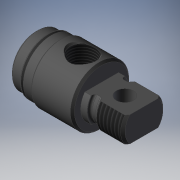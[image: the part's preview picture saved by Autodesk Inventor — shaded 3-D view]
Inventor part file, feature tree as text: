
AUTODESK INVENTOR PART (.ipt)
format: ipt  version: 2019 (Build 230136000, 136)  size: 330,752 bytes
history: native  units: in
note: dims shown in document units (in); Inventor stores cm internally (conversion verified against a paired STEP export)
features: other x168, sketch x7, revolve x4, thread x2, extrude x2, hole x1
ambient origin geometry x8: Origin, YZ Plane, XZ Plane, XY Plane, X Axis, Y Axis, Z Axis, Center Point
bodies: Solid1 (feature_tree)
feature tree (184):
  revolve  "Revolution1"  Angle=360.0deg
  revolve  "Revolution2"  [1 undecoded]
  thread  "Thread1"  [1 undecoded]
  extrude  "Extrusion1"  TaperAngle=360.0deg  [1 undecoded]
  hole  "Hole1"  [1 undecoded]
  revolve  "Revolution3"  [1 undecoded]
  thread  "Thread2"  [1 undecoded]
  revolve  "Revolution4"  [1 undecoded]
  extrude  "Extrusion2"  [1 undecoded]
  other  "1_XY"
  other  "1_YZ"
  other  "1_ZX"
  other  "1_X"
  other  "1_Y"
  other  "1_Z"
  other  "1_Center"
  other  "c1_XY"
  other  "c1_YZ"
  other  "c1_ZX"
  other  "c1_X"
  other  "c1_Y"
  other  "c1_Z"
  other  "c1_Center"
  other  "c2_XY"
  other  "c2_YZ"
  other  "c2_ZX"
  other  "c2_X"
  other  "c2_Y"
  other  "c2_Z"
  other  "c2_Center"
  other  "cc1_XY"
  other  "cc1_YZ"
  other  "cc1_ZX"
  other  "cc1_X"
  other  "cc1_Y"
  other  "cc1_Z"
  other  "cc1_Center"
  other  "cc2_XY"
  other  "cc2_YZ"
  other  "cc2_ZX"
  other  "cc2_X"
  other  "cc2_Y"
  other  "cc2_Z"
  other  "cc2_Center"
  other  "lovra1_XY"
  other  "lovra1_YZ"
  other  "lovra1_ZX"
  other  "lovra1_X"
  other  "lovra1_Y"
  other  "lovra1_Z"
  other  "lovra1_Center"
  other  "lovra2_XY"
  other  "lovra2_YZ"
  other  "lovra2_ZX"
  other  "lovra2_X"
  other  "lovra2_Y"
  other  "lovra2_Z"
  other  "lovra2_Center"
  other  "lovra21_XY"
  other  "lovra21_YZ"
  other  "lovra21_ZX"
  other  "lovra21_X"
  other  "lovra21_Y"
  other  "lovra21_Z"
  other  "lovra21_Center"
  other  "lovra22_XY"
  other  "lovra22_YZ"
  other  "lovra22_ZX"
  other  "lovra22_X"
  other  "lovra22_Y"
  other  "lovra22_Z"
  other  "lovra22_Center"
  other  "lovra3_XY"
  other  "lovra3_YZ"
  other  "lovra3_ZX"
  other  "lovra3_X"
  other  "lovra3_Y"
  other  "lovra3_Z"
  other  "lovra3_Center"
  other  "olen_XY"
  other  "olen_YZ"
  other  "olen_ZX"
  other  "olen_X"
  other  "olen_Y"
  other  "olen_Z"
  other  "olen_Center"
  other  "p1_XY"
  other  "p1_YZ"
  other  "p1_ZX"
  other  "p1_X"
  other  "p1_Y"
  other  "p1_Z"
  other  "p1_Center"
  other  "p2_XY"
  other  "p2_YZ"
  other  "p2_ZX"
  other  "p2_X"
  other  "p2_Y"
  other  "p2_Z"
  other  "p2_Center"
  other  "port_XY"
  other  "port_YZ"
  other  "port_ZX"
  other  "port_X"
  other  "port_Y"
  other  "port_Z"
  other  "port_Center"
  other  "port2_XY"
  other  "port2_YZ"
  other  "port2_ZX"
  other  "port2_X"
  other  "port2_Y"
  other  "port2_Z"
  other  "port2_Center"
  other  "thd1_XY"
  other  "thd1_YZ"
  other  "thd1_ZX"
  other  "thd1_X"
  other  "thd1_Y"
  other  "thd1_Z"
  other  "thd1_Center"
  other  "thd2_XY"
  other  "thd2_YZ"
  other  "thd2_ZX"
  other  "thd2_X"
  other  "thd2_Y"
  other  "thd2_Z"
  other  "thd2_Center"
  other  "to_mounting_bracket_XY"
  other  "to_mounting_bracket_YZ"
  other  "to_mounting_bracket_ZX"
  other  "to_mounting_bracket_X"
  other  "to_mounting_bracket_Y"
  other  "to_mounting_bracket_Z"
  other  "to_mounting_bracket_Center"
  other  "to_nut_XY"
  other  "to_nut_YZ"
  other  "to_nut_ZX"
  other  "to_nut_X"
  other  "to_nut_Y"
  other  "to_nut_Z"
  other  "to_nut_Center"
  other  "to_pin_XY"
  other  "to_pin_YZ"
  other  "to_pin_ZX"
  other  "to_pin_X"
  other  "to_pin_Y"
  other  "to_pin_Z"
  other  "to_pin_Center"
  other  "to_pin_1_XY"
  other  "to_pin_1_YZ"
  other  "to_pin_1_ZX"
  other  "to_pin_1_X"
  other  "to_pin_1_Y"
  other  "to_pin_1_Z"
  other  "to_pin_1_Center"
  other  "to_pin_r_XY"
  other  "to_pin_r_YZ"
  other  "to_pin_r_ZX"
  other  "to_pin_r_X"
  other  "to_pin_r_Y"
  other  "to_pin_r_Z"
  other  "to_pin_r_Center"
  other  "to_screw_XY"
  other  "to_screw_YZ"
  other  "to_screw_ZX"
  other  "to_screw_X"
  other  "to_screw_Y"
  other  "to_screw_Z"
  other  "to_screw_Center"
  other  "to_tube_XY"
  other  "to_tube_YZ"
  other  "to_tube_ZX"
  other  "to_tube_X"
  other  "to_tube_Y"
  other  "to_tube_Z"
  other  "to_tube_Center"
  sketch  "Sketch_8"  dims[d2=0.3547in d3=0.0in d4=0.625in d5=0.0in]
  sketch  "Sketch_15"  dims[d6=0.312in d7=0.75in d8=0.375in d9=0.25in d10=0.5635in d11=0.9284in d12=120.0deg d13=360.0deg]
  sketch  "Sketch_70"
  sketch  "Sketch4"  dims[d0=360.0deg d1=360.0deg]
  sketch  "Sketch_47"  dims[d19=0.0in d20=0.0in d21=0.0in d22=0.0in d23=0.0in d24=0.0in d25=0.0in d26=0.0in]
  sketch  "Sketch_24"  dims[d14=0.2771in d15=0.0in d16=360.0deg]
  sketch  "Sketch_43"  dims[d17=0.5587in d18=0.0in]
note: 8 required parameter values undecoded (feature->parameter linkage not recoverable at this tier; creation-order binding heuristic only, values carry confidence <= 0.55)